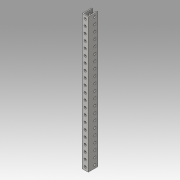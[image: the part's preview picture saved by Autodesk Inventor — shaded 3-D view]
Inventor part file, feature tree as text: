
AUTODESK INVENTOR PART (.ipt)
format: ipt  version: 2016 (Build 200138000, 138)  size: 185,856 bytes
history: native  units: in
note: dims shown in document units (in); Inventor stores cm internally (conversion verified against a paired STEP export)
features: fillet x1
ambient origin geometry x8: Origin, YZ Plane, XZ Plane, XY Plane, X Axis, Y Axis, Z Axis, Center Point
bodies: Solid1 (feature_tree)
feature tree (1):
  fillet  "Fillet1"  [1 undecoded]
note: 1 required parameter value undecoded (feature->parameter linkage not recoverable at this tier; creation-order binding heuristic only, values carry confidence <= 0.55)
